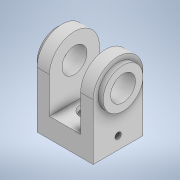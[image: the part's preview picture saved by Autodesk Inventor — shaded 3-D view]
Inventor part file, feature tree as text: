
AUTODESK INVENTOR PART (.ipt)
format: ipt  version: 2021 (Build 250183000, 183)  size: 186,880 bytes
history: native  units: mm
features: extrude x6, sketch x6, fillet x1
ambient origin geometry x8: Origin, YZ Plane, XZ Plane, XY Plane, X Axis, Y Axis, Z Axis, Center Point
bodies: Solid1 (feature_tree)
feature tree (13):
  extrude  "Extrusion1"  Depth=65.0mm
  extrude  "Extrusion2"  Depth=16.0mm
  fillet  "Fillet1"  Radius=22.5mm
  extrude  "Extrusion3"  Depth=32.0mm
  extrude  "Extrusion4"  Depth=22.5mm
  extrude  "Extrusion5"  Depth=20.0mm
  extrude  "Extrusion6"  TaperAngle=0.0deg  [1 undecoded]
  sketch  "Sketch1"  dims[d1=45.0mm d2=65.0mm]
  sketch  "Sketch2"  dims[d3=10.0mm d4=16.0mm d5=22.5mm]
  sketch  "Sketch3"  dims[d6=40.0mm d7=0.0mm d8=32.0mm]
  sketch  "Sketch4"  dims[d9=20.0mm d10=22.5mm]
  sketch  "Sketch5"  dims[d11=4.0mm d12=0.0mm d13=20.0mm]
  sketch  "Sketch6"  dims[d14=16.0mm d15=0.0mm d16=0.0mm d17=32.0mm d18=49.0mm d19=20.0mm d20=4.0mm d21=0.0mm d22=32.0mm d23=49.0mm d24=20.0mm d25=4.0mm d26=0.0mm d27=20.0mm d28=5.0mm d29=10.0mm d30=20.0mm d31=0.0mm d32=0.0mm]
note: 1 required parameter value undecoded (feature->parameter linkage not recoverable at this tier; creation-order binding heuristic only, values carry confidence <= 0.55)
